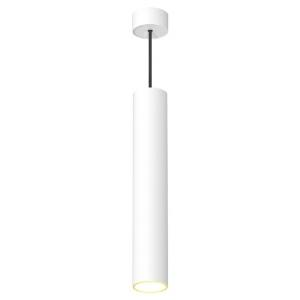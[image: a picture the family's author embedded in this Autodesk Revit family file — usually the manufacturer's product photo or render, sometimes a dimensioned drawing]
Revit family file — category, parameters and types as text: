
# Revit family: hangover_810-0500-H30-K20
name_source: partatom
category: Leuchten
revit_build: Autodesk Revit 2018 (Build: 20190510_1515(x64)
units: mm (PartAtom-declared; Revit-internal decimal feet)

## family parameters
Basisbauteil = Fläche
Beim Laden mit Abzugskörper schneiden = Nein
Bemaßung runder Anschluss = Durchmesser verwenden
Gemeinsam genutzt = Nein
Lichtquelle = Nein
Raumberechnungspunkt = Nein
Teiletyp = Normal

## types (1)
- 810-0500-H30-K20-L00
    Beschreibung = HANGOVER
    CIE Flux Codes = 90 96 99 100 85
    Color Rendering = 1A/90…99
    Color Temperature = 3000K
    Height = 450 mm
    Hersteller = Prolicht
    Lamp Light Flux = 1782 lm
    Lamp Power = 20 W
    Lamp count = 1
    Lampe = 1 x LED
    Length = 75 mm
    Luminous efficacy = 76 lm/W
    ModVariant = Nein
    Modell = 810-0500
    Mounting Place = Ceiling
    Mounting Type = Pendant
    Number of Poles = 1
    OnlyDefault = Ja
    Power Factor = 1
    Product Name = HANGOVER
    Product group = Suspended spotlights
    ProductGroupID = 942
    Protection Class = Protection class
    Protection Degree = Degree of protection
    RLX_Detail_Level = 1
    Scheinlast = 20 VA
    Socket = socket
    Standby Power = 0 W
    System Light Flux = 1512 lm
    System Power = 20 W
    Typenbild = 410-7590.jpg
    Typenkommentare = LED COLOUR DIR 2700 K (27),REFLECTOR 20° (20),SHINE RING ABSICHTLICH_LEER (00)
    URL = http://prolicht.at
    VarID = 810-0500-h30-k20-l00
    Voltage = 0 V
    Vorgabe-Ansicht = 1800 mm
    Weight = 0.00 kg
    Width = 0 mm  [stored 0 ft]

note: [stored X ft] marks values corroborated as IEEE doubles in the binary element streams (Revit-internal decimal feet)

## geometry (parser evidence)
native form markers: Sweep x7
no freeform markers — native parametric forms only
